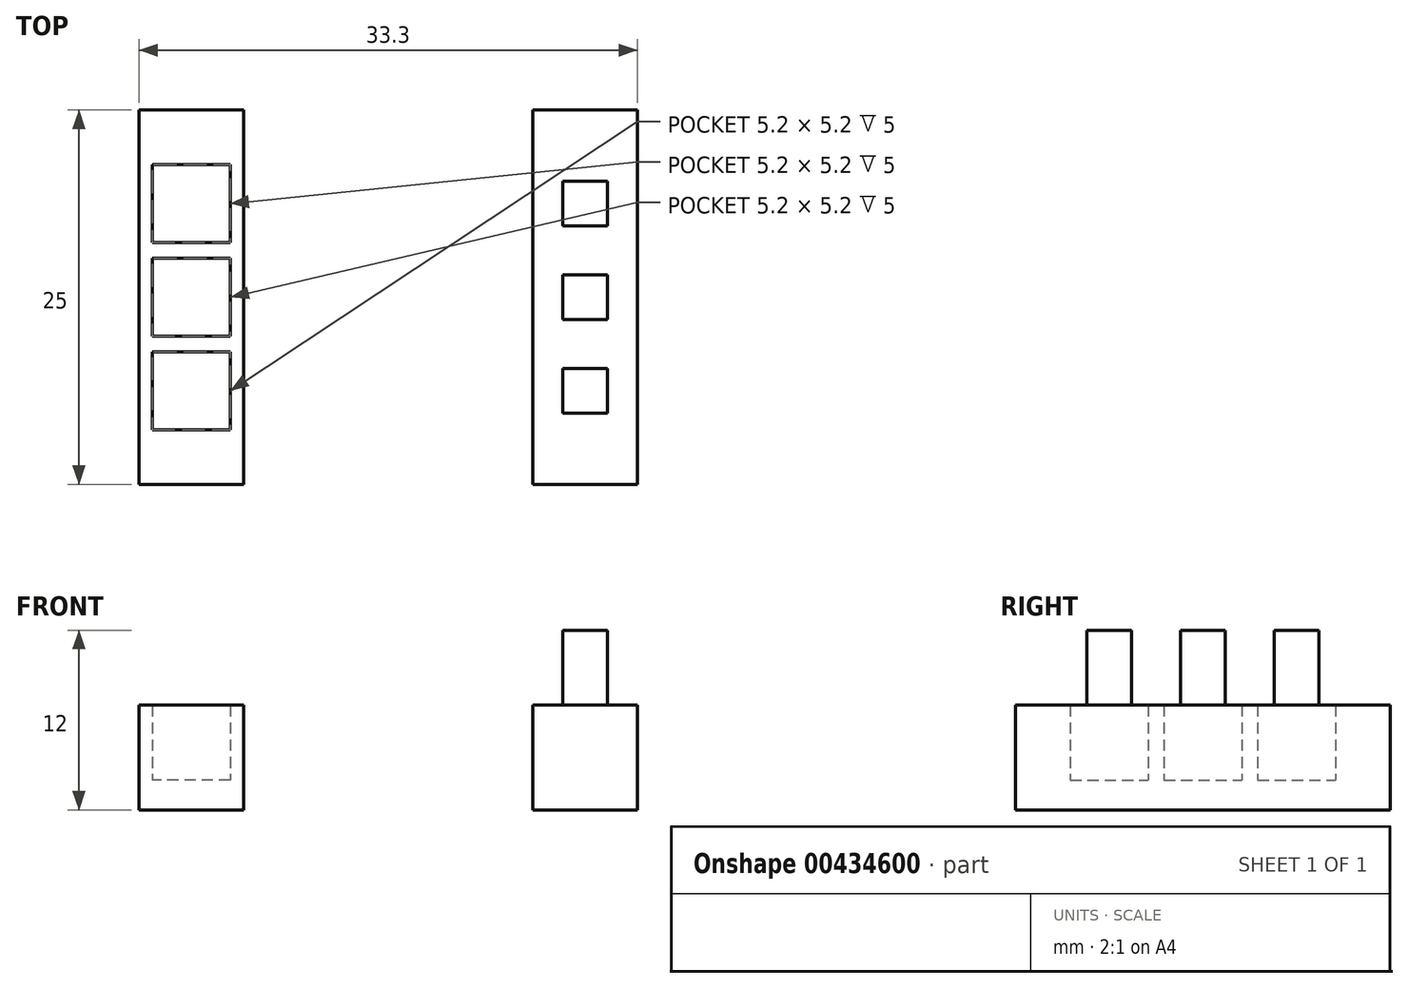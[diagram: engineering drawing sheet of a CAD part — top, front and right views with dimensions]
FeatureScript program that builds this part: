
annotation { "Feature Type Name" : "Feature", "Feature Type Description" : "" }
export const myFeature = defineFeature(function(context is Context, id is Id, definition is map)
    precondition{}
    {
        {
            var Q0;
            Q0=qCreatedBy(makeId("Top.planeOp"),FACE);
            var sketch = newSketch(context, id + "F0", { "sketchPlane" : qUnion([Q0])});
            skLineSegment(sketch, "E0.bottom", {"start": v(0.8, 14) * mm, "end": v(7.8, 14) * mm});
            skLineSegment(sketch, "E0.top", {"start": v(0.8, -11) * mm, "end": v(7.8, -11) * mm});
            skLineSegment(sketch, "E0.left", {"start": v(0.8, 14) * mm, "end": v(0.8, 1.5) * mm});
            skLineSegment(sketch, "E0.right", {"start": v(7.8, 14) * mm, "end": v(7.8, -11) * mm});
            skLineSegment(sketch, "E1.bottom", {"start": v(5.8, 6.25) * mm, "end": v(2.8, 6.25) * mm});
            skLineSegment(sketch, "E1.top", {"start": v(5.8, 9.25) * mm, "end": v(2.8, 9.25) * mm});
            skLineSegment(sketch, "E1.left", {"start": v(5.8, 6.25) * mm, "end": v(5.8, 9.25) * mm});
            skLineSegment(sketch, "E1.right", {"start": v(2.8, 6.25) * mm, "end": v(2.8, 9.25) * mm});
            skPoint(sketch, "E1.middle", {"position": v(4.3, 7.75) * mm});
            skLineSegment(sketch, "E2", {"start": v(4.3, 14) * mm, "end": v(4.3, -11) * mm, "construction": true});
            skLineSegment(sketch, "E3", {"start": v(0.8, 1.5) * mm, "end": v(7.8, 1.5) * mm, "construction": true});
            skLineSegment(sketch, "E4", {"start": v(0.8, 1.5) * mm, "end": v(0.8, -11) * mm});
            skPoint(sketch, "E5", {"position": v(0.8, 7.75) * mm});
            skPoint(sketch, "E6", {"position": v(0.8, -4.75) * mm});
            skPoint(sketch, "E7", {"position": v(4.3, -4.75) * mm});
            skLineSegment(sketch, "E8.bottom", {"start": v(5.8, -6.25) * mm, "end": v(2.8, -6.25) * mm});
            skLineSegment(sketch, "E8.top", {"start": v(5.8, -3.25) * mm, "end": v(2.8, -3.25) * mm});
            skLineSegment(sketch, "E8.left", {"start": v(5.8, -6.25) * mm, "end": v(5.8, -3.25) * mm});
            skLineSegment(sketch, "E8.right", {"start": v(2.8, -6.25) * mm, "end": v(2.8, -3.25) * mm});
            skLineSegment(sketch, "E9.bottom", {"start": v(5.8, 0) * mm, "end": v(2.8, 0) * mm});
            skLineSegment(sketch, "E9.top", {"start": v(5.8, 3) * mm, "end": v(2.8, 3) * mm});
            skLineSegment(sketch, "E9.left", {"start": v(5.8, 0) * mm, "end": v(5.8, 3) * mm});
            skLineSegment(sketch, "E9.right", {"start": v(2.8, 0) * mm, "end": v(2.8, 3) * mm});
            skPoint(sketch, "E9.middle", {"position": v(4.3, 1.5) * mm});
            skLineSegment(sketch, "E10.bottom", {"start": v(6.9, 5.15) * mm, "end": v(1.7, 5.15) * mm});
            skLineSegment(sketch, "E10.top", {"start": v(6.9, 10.35) * mm, "end": v(1.7, 10.35) * mm});
            skLineSegment(sketch, "E10.left", {"start": v(6.9, 5.15) * mm, "end": v(6.9, 10.35) * mm});
            skLineSegment(sketch, "E10.right", {"start": v(1.7, 5.15) * mm, "end": v(1.7, 10.35) * mm});
            skLineSegment(sketch, "E11.bottom", {"start": v(6.9, -1.1) * mm, "end": v(1.7, -1.1) * mm});
            skLineSegment(sketch, "E11.top", {"start": v(6.9, 4.1) * mm, "end": v(1.7, 4.1) * mm});
            skLineSegment(sketch, "E11.left", {"start": v(6.9, -1.1) * mm, "end": v(6.9, 4.1) * mm});
            skLineSegment(sketch, "E11.right", {"start": v(1.7, -1.1) * mm, "end": v(1.7, 4.1) * mm});
            skLineSegment(sketch, "E12.bottom", {"start": v(6.9, -7.35) * mm, "end": v(1.7, -7.35) * mm});
            skLineSegment(sketch, "E12.top", {"start": v(6.9, -2.15) * mm, "end": v(1.7, -2.15) * mm});
            skLineSegment(sketch, "E12.left", {"start": v(6.9, -7.35) * mm, "end": v(6.9, -2.15) * mm});
            skLineSegment(sketch, "E12.right", {"start": v(1.7, -7.35) * mm, "end": v(1.7, -2.15) * mm});
            skSolve(sketch);
        }
        {
            var Q0;
            Q0 = qSketchRegion(id + "F0", true);
            var Q1;
            Q1=makeQuery(id+"F0.imprint","IMPRINT",FACE,{"disambiguationData":[TD([[makeQuery(id+"F0.imprint","IMPRINT",EDGE,{"derivedFrom":sQuery(id+"F0.wireOp",EDGE,"E1.bottom")}),-1.0]])]});
            var Q2;
            Q2=makeQuery(id+"F0.imprint","IMPRINT",FACE,{"disambiguationData":[TD([[makeQuery(id+"F0.imprint","IMPRINT",EDGE,{"derivedFrom":sQuery(id+"F0.wireOp",EDGE,"E9.bottom")}),-1.0]])]});
            var Q3;
            Q3=makeQuery(id+"F0.imprint","IMPRINT",FACE,{"disambiguationData":[TD([[makeQuery(id+"F0.imprint","IMPRINT",EDGE,{"derivedFrom":sQuery(id+"F0.wireOp",EDGE,"E8.bottom")}),-1.0]])]});
            var Q4;
            Q4=makeQuery(id+"F0.imprint","IMPRINT",FACE,{"disambiguationData":[TD([[makeQuery(id+"F0.imprint","IMPRINT",EDGE,{"derivedFrom":sQuery(id+"F0.wireOp",EDGE,"E1.bottom")}),1.0]])]});
            var Q5;
            Q5=makeQuery(id+"F0.imprint","IMPRINT",FACE,{"disambiguationData":[TD([[makeQuery(id+"F0.imprint","IMPRINT",EDGE,{"derivedFrom":sQuery(id+"F0.wireOp",EDGE,"E9.bottom")}),1.0]])]});
            var Q6;
            Q6=makeQuery(id+"F0.imprint","IMPRINT",FACE,{"disambiguationData":[TD([[makeQuery(id+"F0.imprint","IMPRINT",EDGE,{"derivedFrom":sQuery(id+"F0.wireOp",EDGE,"E8.bottom")}),1.0]])]});
            extrude(context, id + "F1", {"entities" : qUnion([Q0, Q1, Q2, Q3, Q4, Q5, Q6]), "depth" : 7 * mm});
        }
        {
            var Q0;
            Q0=makeQuery(id+"F0.imprint","IMPRINT",FACE,{"disambiguationData":[TD([[makeQuery(id+"F0.imprint","IMPRINT",EDGE,{"derivedFrom":sQuery(id+"F0.wireOp",EDGE,"E1.bottom")}),-1.0]])]});
            var Q1;
            Q1=makeQuery(id+"F0.imprint","IMPRINT",FACE,{"disambiguationData":[TD([[makeQuery(id+"F0.imprint","IMPRINT",EDGE,{"derivedFrom":sQuery(id+"F0.wireOp",EDGE,"E9.bottom")}),-1.0]])]});
            var Q2;
            Q2=makeQuery(id+"F0.imprint","IMPRINT",FACE,{"disambiguationData":[TD([[makeQuery(id+"F0.imprint","IMPRINT",EDGE,{"derivedFrom":sQuery(id+"F0.wireOp",EDGE,"E8.bottom")}),-1.0]])]});
            extrude(context, id + "F2", {"entities" : qUnion([Q0, Q1, Q2]), "operationType" : NewBodyOperationType.ADD, "depth" : 12 * mm});
        }
        {
            var Q0;
            Q0=makeQuery(id+"F1.opExtrude","SWEPT_BODY",BODY,{"disambiguationData":[OSD([sQuery(id+"F0.wireOp",EDGE,"E0.bottom"),sQuery(id+"F0.wireOp",EDGE,"E0.top"),sQuery(id+"F0.wireOp",EDGE,"E0.left"),sQuery(id+"F0.wireOp",EDGE,"E0.right"),sQuery(id+"F0.wireOp",EDGE,"E4")])]});
            transform(context, id + "F3", {"entities" : qUnion([Q0]), "transformType" : TransformType.TRANSLATION_3D, "dx" : 26.3 * mm, "dy" : 0 * mm, "dz" : 0 * mm, "makeCopy" : false});
        }
        {
            var Q0;
            Q0=makeQuery(id+"F0.imprint","IMPRINT",FACE,{"disambiguationData":[TD([[makeQuery(id+"F0.imprint","IMPRINT",EDGE,{"derivedFrom":sQuery(id+"F0.wireOp",EDGE,"E0.bottom")}),-1.0]])]});
            extrude(context, id + "F4", {"entities" : qUnion([Q0]), "depth" : 7 * mm});
        }
        {
            var Q0;
            Q0 = qSketchRegion(id + "F0", true);
            var Q1;
            Q1=makeQuery(id+"F0.imprint","IMPRINT",FACE,{"disambiguationData":[TD([[makeQuery(id+"F0.imprint","IMPRINT",EDGE,{"derivedFrom":sQuery(id+"F0.wireOp",EDGE,"E1.bottom")}),-1.0]])]});
            var Q2;
            Q2=makeQuery(id+"F0.imprint","IMPRINT",FACE,{"disambiguationData":[TD([[makeQuery(id+"F0.imprint","IMPRINT",EDGE,{"derivedFrom":sQuery(id+"F0.wireOp",EDGE,"E1.bottom")}),1.0]])]});
            var Q3;
            Q3=makeQuery(id+"F0.imprint","IMPRINT",FACE,{"disambiguationData":[TD([[makeQuery(id+"F0.imprint","IMPRINT",EDGE,{"derivedFrom":sQuery(id+"F0.wireOp",EDGE,"E9.bottom")}),1.0]])]});
            var Q4;
            Q4=makeQuery(id+"F0.imprint","IMPRINT",FACE,{"disambiguationData":[TD([[makeQuery(id+"F0.imprint","IMPRINT",EDGE,{"derivedFrom":sQuery(id+"F0.wireOp",EDGE,"E9.bottom")}),-1.0]])]});
            var Q5;
            Q5=makeQuery(id+"F0.imprint","IMPRINT",FACE,{"disambiguationData":[TD([[makeQuery(id+"F0.imprint","IMPRINT",EDGE,{"derivedFrom":sQuery(id+"F0.wireOp",EDGE,"E8.bottom")}),1.0]])]});
            var Q6;
            Q6=makeQuery(id+"F0.imprint","IMPRINT",FACE,{"disambiguationData":[TD([[makeQuery(id+"F0.imprint","IMPRINT",EDGE,{"derivedFrom":sQuery(id+"F0.wireOp",EDGE,"E8.bottom")}),-1.0]])]});
            extrude(context, id + "F5", {"entities" : qUnion([Q0, Q1, Q2, Q3, Q4, Q5, Q6]), "operationType" : NewBodyOperationType.ADD, "depth" : 2 * mm});
        }
    });
